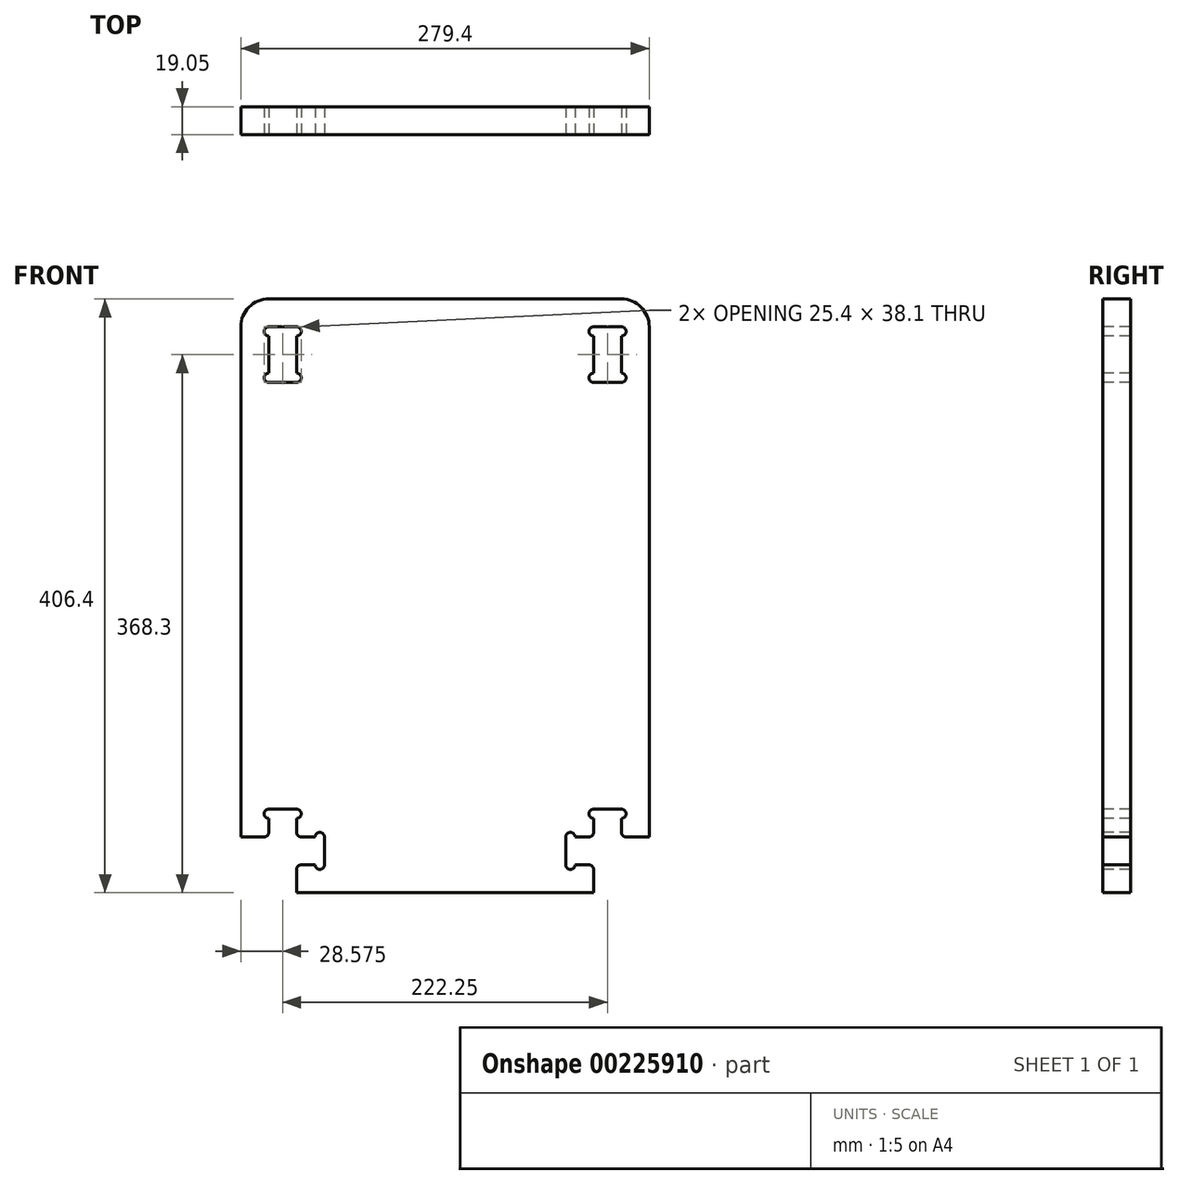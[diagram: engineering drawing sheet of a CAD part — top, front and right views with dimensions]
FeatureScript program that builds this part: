
annotation { "Feature Type Name" : "Feature", "Feature Type Description" : "" }
export const myFeature = defineFeature(function(context is Context, id is Id, definition is map)
    precondition{}
    {
        {
            var Q0;
            Q0=qCreatedBy(makeId("Front.planeOp"),FACE);
            var sketch = newSketch(context, id + "F0", { "sketchPlane" : qUnion([Q0])});
            skLineSegment(sketch, "E0.bottom", {"start": v(0, 0) * mm, "end": v(279.4, 0) * mm});
            skLineSegment(sketch, "E0.top", {"start": v(0, 406.4) * mm, "end": v(279.4, 406.4) * mm});
            skLineSegment(sketch, "E0.left", {"start": v(0, 0) * mm, "end": v(0, 406.4) * mm});
            skLineSegment(sketch, "E0.right", {"start": v(279.4, 0) * mm, "end": v(279.4, 406.4) * mm});
            skSolve(sketch);
        }
        {
            var Q0;
            Q0 = qSketchRegion(id + "F0", true);
            extrude(context, id + "F1", {"entities" : qUnion([Q0]), "depth" : 19.05 * mm});
        }
        {
            var Q0;
            Q0=makeQuery(id+"F1.opExtrude","SWEPT_EDGE",EDGE,{"disambiguationData":[OSD([sQuery(id+"F0.wireOp",EDGE,"E0.top"),sQuery(id+"F0.wireOp",EDGE,"E0.left")])]});
            var Q1;
            Q1=makeQuery(id+"F1.opExtrude","SWEPT_EDGE",EDGE,{"disambiguationData":[OSD([sQuery(id+"F0.wireOp",EDGE,"E0.top"),sQuery(id+"F0.wireOp",EDGE,"E0.right")])]});
            fillet(context, id + "F2", {"entities" : qUnion([Q0, Q1]), "radius" : 19.05 * mm, "tangentPropagation" : true, "allowEdgeOverflow" : false});
        }
        {
            var Q0;
            Q0=makeQuery(id+"F1.opExtrude","CAP_FACE",FACE,{"disambiguationData":[OSD([sQuery(id+"F0.wireOp",EDGE,"E0.bottom"),sQuery(id+"F0.wireOp",EDGE,"E0.top"),sQuery(id+"F0.wireOp",EDGE,"E0.left"),sQuery(id+"F0.wireOp",EDGE,"E0.right")])],"isStart":false});
            var sketch = newSketch(context, id + "F3", { "sketchPlane" : qUnion([Q0])});
            skLineSegment(sketch, "E1", {"start": v(38.1, 0) * mm, "end": v(38.1, 19.05) * mm});
            skLineSegment(sketch, "E2", {"start": v(38.1, 19.05) * mm, "end": v(57.15, 19.05) * mm});
            skLineSegment(sketch, "E3", {"start": v(57.15, 19.05) * mm, "end": v(57.15, 38.1) * mm});
            skLineSegment(sketch, "E4", {"start": v(57.15, 38.1) * mm, "end": v(38.1, 38.1) * mm});
            skLineSegment(sketch, "E5", {"start": v(38.1, 38.1) * mm, "end": v(38.1, 57.15) * mm});
            skLineSegment(sketch, "E6", {"start": v(38.1, 57.15) * mm, "end": v(19.05, 57.15) * mm});
            skLineSegment(sketch, "E7", {"start": v(19.05, 57.15) * mm, "end": v(19.05, 38.1) * mm});
            skLineSegment(sketch, "E8", {"start": v(19.05, 38.1) * mm, "end": v(0, 38.1) * mm});
            skLineSegment(sketch, "E9", {"start": v(0, 38.1) * mm, "end": v(0, 0) * mm});
            skLineSegment(sketch, "E10", {"start": v(0, 0) * mm, "end": v(38.1, 0) * mm});
            skLineSegment(sketch, "E11", {"start": v(241.3, 0) * mm, "end": v(241.3, 19.05) * mm});
            skLineSegment(sketch, "E12", {"start": v(241.3, 19.05) * mm, "end": v(222.25, 19.05) * mm});
            skLineSegment(sketch, "E13", {"start": v(222.25, 19.05) * mm, "end": v(222.25, 38.1) * mm});
            skLineSegment(sketch, "E14", {"start": v(222.25, 38.1) * mm, "end": v(241.3, 38.1) * mm});
            skLineSegment(sketch, "E15", {"start": v(241.3, 38.1) * mm, "end": v(241.3, 57.15) * mm});
            skLineSegment(sketch, "E16", {"start": v(241.3, 57.15) * mm, "end": v(260.35, 57.15) * mm});
            skLineSegment(sketch, "E17", {"start": v(260.35, 57.15) * mm, "end": v(260.35, 38.1) * mm});
            skLineSegment(sketch, "E18", {"start": v(260.35, 38.1) * mm, "end": v(279.4, 38.1) * mm});
            skLineSegment(sketch, "E19", {"start": v(279.4, 38.1) * mm, "end": v(279.4, 0) * mm});
            skLineSegment(sketch, "E20", {"start": v(279.4, 0) * mm, "end": v(241.3, 0) * mm});
            skSolve(sketch);
        }
        {
            var Q0;
            Q0 = qSketchRegion(id + "F3", true);
            extrude(context, id + "F4", {"entities" : qUnion([Q0]), "operationType" : NewBodyOperationType.REMOVE, "oppositeDirection" : true, "depth" : 19.05 * mm});
        }
        {
            var Q0;
            Q0=makeQuery(id+"F1.opExtrude","CAP_FACE",FACE,{"disambiguationData":[OSD([sQuery(id+"F0.wireOp",EDGE,"E0.bottom"),sQuery(id+"F0.wireOp",EDGE,"E0.top"),sQuery(id+"F0.wireOp",EDGE,"E0.left"),sQuery(id+"F0.wireOp",EDGE,"E0.right")])],"isStart":false});
            var sketch = newSketch(context, id + "F5", { "sketchPlane" : qUnion([Q0])});
            skArc(sketch, "E21", {"start": v(19.05, 57.15) * mm, "mid": v(15.87, 53.97) * mm, "end": v(19.05, 50.8) * mm});
            skArc(sketch, "E22", {"start": v(38.1, 57.15) * mm, "mid": v(41.27, 53.97) * mm, "end": v(38.1, 50.8) * mm});
            skArc(sketch, "E23", {"start": v(57.15, 38.1) * mm, "mid": v(53.98, 41.27) * mm, "end": v(50.8, 38.1) * mm});
            skArc(sketch, "E24", {"start": v(57.15, 19.05) * mm, "mid": v(53.97, 15.87) * mm, "end": v(50.8, 19.05) * mm});
            skArc(sketch, "E25", {"start": v(222.25, 19.05) * mm, "mid": v(225.43, 15.87) * mm, "end": v(228.6, 19.05) * mm});
            skArc(sketch, "E26", {"start": v(222.25, 38.1) * mm, "mid": v(225.43, 41.27) * mm, "end": v(228.6, 38.1) * mm});
            skArc(sketch, "E27", {"start": v(241.3, 57.15) * mm, "mid": v(238.12, 53.97) * mm, "end": v(241.3, 50.8) * mm});
            skArc(sketch, "E28", {"start": v(260.35, 57.15) * mm, "mid": v(263.53, 53.97) * mm, "end": v(260.35, 50.8) * mm});
            skLineSegment(sketch, "E29", {"start": v(19.05, 57.15) * mm, "end": v(19.05, 50.8) * mm});
            skLineSegment(sketch, "E30", {"start": v(38.1, 50.8) * mm, "end": v(38.1, 57.15) * mm});
            skLineSegment(sketch, "E31", {"start": v(50.8, 38.1) * mm, "end": v(57.15, 38.1) * mm});
            skLineSegment(sketch, "E32", {"start": v(50.8, 19.05) * mm, "end": v(57.15, 19.05) * mm});
            skLineSegment(sketch, "E33", {"start": v(222.25, 38.1) * mm, "end": v(228.6, 38.1) * mm});
            skLineSegment(sketch, "E34", {"start": v(222.25, 19.05) * mm, "end": v(228.6, 19.05) * mm});
            skLineSegment(sketch, "E35", {"start": v(241.3, 57.15) * mm, "end": v(241.3, 50.8) * mm});
            skLineSegment(sketch, "E36", {"start": v(260.35, 57.15) * mm, "end": v(260.35, 50.8) * mm});
            skSolve(sketch);
        }
        {
            var Q0;
            Q0 = qSketchRegion(id + "F5", true);
            extrude(context, id + "F6", {"entities" : qUnion([Q0]), "operationType" : NewBodyOperationType.REMOVE, "oppositeDirection" : true, "depth" : 19.05 * mm});
        }
        {
            var Q0;
            Q0=makeQuery(id+"F1.opExtrude","CAP_FACE",FACE,{"disambiguationData":[OSD([sQuery(id+"F0.wireOp",EDGE,"E0.bottom"),sQuery(id+"F0.wireOp",EDGE,"E0.top"),sQuery(id+"F0.wireOp",EDGE,"E0.left"),sQuery(id+"F0.wireOp",EDGE,"E0.right")])],"isStart":false});
            var sketch = newSketch(context, id + "F7", { "sketchPlane" : qUnion([Q0])});
            skLineSegment(sketch, "E37.bottom", {"start": v(19.05, 387.35) * mm, "end": v(38.1, 387.35) * mm});
            skLineSegment(sketch, "E37.top", {"start": v(19.05, 349.25) * mm, "end": v(38.1, 349.25) * mm});
            skLineSegment(sketch, "E37.left", {"start": v(19.05, 387.35) * mm, "end": v(19.05, 349.25) * mm});
            skLineSegment(sketch, "E37.right", {"start": v(38.1, 387.35) * mm, "end": v(38.1, 349.25) * mm});
            skLineSegment(sketch, "E38.bottom", {"start": v(260.35, 387.35) * mm, "end": v(241.3, 387.35) * mm});
            skLineSegment(sketch, "E38.top", {"start": v(260.35, 349.25) * mm, "end": v(241.3, 349.25) * mm});
            skLineSegment(sketch, "E38.left", {"start": v(260.35, 387.35) * mm, "end": v(260.35, 349.25) * mm});
            skLineSegment(sketch, "E38.right", {"start": v(241.3, 387.35) * mm, "end": v(241.3, 349.25) * mm});
            skSolve(sketch);
        }
        {
            var Q0;
            Q0 = qSketchRegion(id + "F7", true);
            extrude(context, id + "F8", {"entities" : qUnion([Q0]), "operationType" : NewBodyOperationType.REMOVE, "oppositeDirection" : true, "depth" : 19.05 * mm});
        }
        {
            var Q0;
            Q0=makeQuery(id+"F1.opExtrude","CAP_FACE",FACE,{"disambiguationData":[OSD([sQuery(id+"F0.wireOp",EDGE,"E0.bottom"),sQuery(id+"F0.wireOp",EDGE,"E0.top"),sQuery(id+"F0.wireOp",EDGE,"E0.left"),sQuery(id+"F0.wireOp",EDGE,"E0.right")])],"isStart":false});
            var sketch = newSketch(context, id + "F9", { "sketchPlane" : qUnion([Q0])});
            skArc(sketch, "E39", {"start": v(19.05, 387.35) * mm, "mid": v(15.87, 384.18) * mm, "end": v(19.05, 381) * mm});
            skArc(sketch, "E40", {"start": v(19.05, 349.25) * mm, "mid": v(15.87, 352.42) * mm, "end": v(19.05, 355.6) * mm});
            skArc(sketch, "E41", {"start": v(38.1, 349.25) * mm, "mid": v(41.28, 352.42) * mm, "end": v(38.1, 355.6) * mm});
            skArc(sketch, "E42", {"start": v(38.1, 387.35) * mm, "mid": v(41.28, 384.18) * mm, "end": v(38.1, 381) * mm});
            skArc(sketch, "E43", {"start": v(241.3, 387.35) * mm, "mid": v(238.12, 384.18) * mm, "end": v(241.3, 381) * mm});
            skArc(sketch, "E44", {"start": v(260.35, 387.35) * mm, "mid": v(263.52, 384.18) * mm, "end": v(260.35, 381) * mm});
            skArc(sketch, "E45", {"start": v(241.3, 349.25) * mm, "mid": v(238.12, 352.42) * mm, "end": v(241.3, 355.6) * mm});
            skArc(sketch, "E46", {"start": v(260.35, 349.25) * mm, "mid": v(263.52, 352.42) * mm, "end": v(260.35, 355.6) * mm});
            skLineSegment(sketch, "E47", {"start": v(260.35, 355.6) * mm, "end": v(260.35, 349.25) * mm});
            skLineSegment(sketch, "E48", {"start": v(241.3, 349.25) * mm, "end": v(241.3, 355.6) * mm});
            skLineSegment(sketch, "E49", {"start": v(241.3, 387.35) * mm, "end": v(241.3, 381) * mm});
            skLineSegment(sketch, "E50", {"start": v(260.35, 381) * mm, "end": v(260.35, 387.35) * mm});
            skLineSegment(sketch, "E51", {"start": v(19.05, 387.35) * mm, "end": v(19.05, 381) * mm});
            skLineSegment(sketch, "E52", {"start": v(38.1, 381) * mm, "end": v(38.1, 387.35) * mm});
            skLineSegment(sketch, "E53", {"start": v(19.05, 355.6) * mm, "end": v(19.05, 349.25) * mm});
            skLineSegment(sketch, "E54", {"start": v(38.1, 349.25) * mm, "end": v(38.1, 355.6) * mm});
            skSolve(sketch);
        }
        {
            var Q0;
            Q0 = qSketchRegion(id + "F9", true);
            extrude(context, id + "F10", {"entities" : qUnion([Q0]), "operationType" : NewBodyOperationType.REMOVE, "oppositeDirection" : true, "depth" : 19.05 * mm});
        }
        {
            var Q0;
            Q0=makeQuery(id+"F4.boolean.opBoolean","COPY",EDGE,{"derivedFrom":makeQuery(id+"F4.opExtrude","SWEPT_EDGE",EDGE,{"disambiguationData":[OSD([sQuery(id+"F0.wireOp",EDGE,"E0.left"),sQuery(id+"F3.wireOp",EDGE,"E8"),sQuery(id+"F3.wireOp",EDGE,"E9")])]})});
            var Q1;
            Q1=makeQuery(id+"F4.boolean.opBoolean","COPY",EDGE,{"derivedFrom":makeQuery(id+"F4.opExtrude","SWEPT_EDGE",EDGE,{"disambiguationData":[OSD([sQuery(id+"F3.wireOp",EDGE,"E7"),sQuery(id+"F3.wireOp",EDGE,"E8")])]})});
            var Q2;
            Q2=makeQuery(id+"F4.boolean.opBoolean","COPY",EDGE,{"derivedFrom":makeQuery(id+"F4.opExtrude","SWEPT_EDGE",EDGE,{"disambiguationData":[OSD([sQuery(id+"F3.wireOp",EDGE,"E4"),sQuery(id+"F3.wireOp",EDGE,"E5")])]})});
            var Q3;
            Q3=makeQuery(id+"F4.boolean.opBoolean","COPY",EDGE,{"derivedFrom":makeQuery(id+"F4.opExtrude","SWEPT_EDGE",EDGE,{"disambiguationData":[OSD([sQuery(id+"F0.wireOp",EDGE,"E0.bottom"),sQuery(id+"F3.wireOp",EDGE,"E1"),sQuery(id+"F3.wireOp",EDGE,"E10")])]})});
            var Q4;
            Q4=makeQuery(id+"F4.boolean.opBoolean","COPY",EDGE,{"derivedFrom":makeQuery(id+"F4.opExtrude","SWEPT_EDGE",EDGE,{"disambiguationData":[OSD([sQuery(id+"F0.wireOp",EDGE,"E0.bottom"),sQuery(id+"F3.wireOp",EDGE,"E11"),sQuery(id+"F3.wireOp",EDGE,"E20")])]})});
            var Q5;
            Q5=makeQuery(id+"F4.boolean.opBoolean","COPY",EDGE,{"derivedFrom":makeQuery(id+"F4.opExtrude","SWEPT_EDGE",EDGE,{"disambiguationData":[OSD([sQuery(id+"F3.wireOp",EDGE,"E11"),sQuery(id+"F3.wireOp",EDGE,"E12")])]})});
            var Q6;
            Q6=makeQuery(id+"F4.boolean.opBoolean","COPY",EDGE,{"derivedFrom":makeQuery(id+"F4.opExtrude","SWEPT_EDGE",EDGE,{"disambiguationData":[OSD([sQuery(id+"F3.wireOp",EDGE,"E14"),sQuery(id+"F3.wireOp",EDGE,"E15")])]})});
            var Q7;
            Q7=makeQuery(id+"F4.boolean.opBoolean","COPY",EDGE,{"derivedFrom":makeQuery(id+"F4.opExtrude","SWEPT_EDGE",EDGE,{"disambiguationData":[OSD([sQuery(id+"F3.wireOp",EDGE,"E17"),sQuery(id+"F3.wireOp",EDGE,"E18")])]})});
            var Q8;
            Q8=makeQuery(id+"F4.boolean.opBoolean","COPY",EDGE,{"derivedFrom":makeQuery(id+"F4.opExtrude","SWEPT_EDGE",EDGE,{"disambiguationData":[OSD([sQuery(id+"F0.wireOp",EDGE,"E0.right"),sQuery(id+"F3.wireOp",EDGE,"E18"),sQuery(id+"F3.wireOp",EDGE,"E19")])]})});
            var Q9;
            Q9=makeQuery(id+"F4.boolean.opBoolean","COPY",EDGE,{"derivedFrom":makeQuery(id+"F4.opExtrude","SWEPT_EDGE",EDGE,{"disambiguationData":[OSD([sQuery(id+"F3.wireOp",EDGE,"E1"),sQuery(id+"F3.wireOp",EDGE,"E2")])]})});
            fillet(context, id + "F11", {"entities" : qUnion([Q0, Q1, Q2, Q3, Q4, Q5, Q6, Q7, Q8, Q9]), "radius" : 3.17 * mm, "tangentPropagation" : true, "allowEdgeOverflow" : false});
        }
    });
